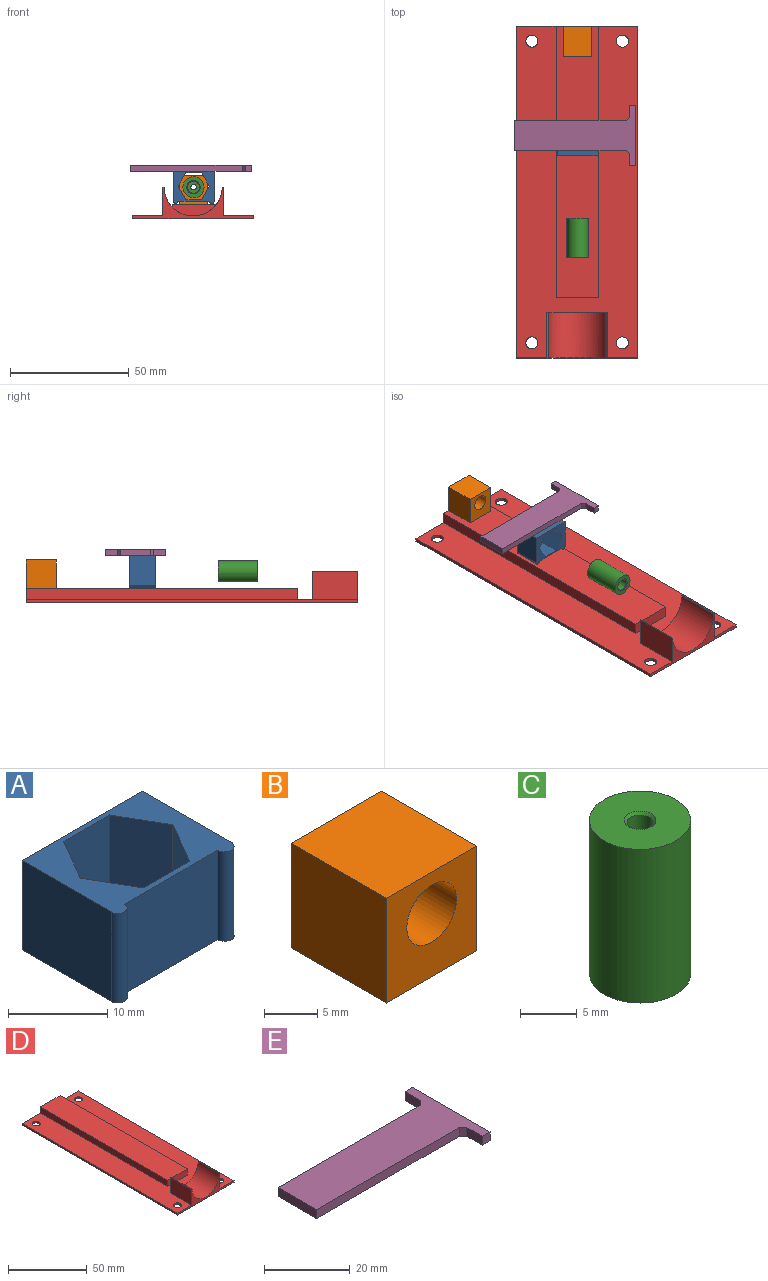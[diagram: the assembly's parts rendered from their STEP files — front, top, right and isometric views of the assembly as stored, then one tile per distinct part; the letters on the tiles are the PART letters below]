
ASSEMBLY  parts=5 mates=4
PART A: 14 faces, bbox 17.1x13.7x11 mm
  f0: plane 17.15x11.05mm, normal (0,1,0), area 189.4mm2, adj f1,f11,f12,f13
  f1: plane 12.7x11.05mm, normal (-1,0,0), area 140.3mm2, adj f0,f2,f12,f13
  f2: cylinder r=0.95mm len=11.05mm, axis (0,0,-1), area 33.1mm2, adj f1,f3,f12,f13
  f3: plane 13.34x11.05mm, normal (0,-1,0), area 147.3mm2, adj f2,f4,f12,f13
  f4: cylinder r=0.95mm len=11.05mm, axis (0,0,-1), area 33.1mm2, adj f3,f11,f12,f13
  f5: plane 11.05x5.72mm, normal (-0.87,0.5,0), area 72.9mm2, adj f6,f10,f12,f13
  f6: plane 11.05x6.6mm, normal (0,1,0), area 72.9mm2, adj f5,f7,f12,f13
  f7: plane 11.05x5.72mm, normal (0.87,0.5,0), area 72.9mm2, adj f6,f8,f12,f13
  f8: plane 11.05x5.72mm, normal (0.87,-0.5,0), area 72.9mm2, adj f7,f9,f12,f13
  f9: plane 11.05x6.6mm, normal (0,-1,0), area 72.9mm2, adj f8,f10,f12,f13
  f10: plane 11.05x5.72mm, normal (-0.87,-0.5,0), area 72.9mm2, adj f5,f9,f12,f13
  f11: plane 12.7x11.05mm, normal (1,0,0), area 140.3mm2, adj f0,f4,f12,f13
  f12: plane 17.15x13.65mm, normal (0,0,1), area 107.4mm2, adj f0,f1,f2,f3,f4,f5,f6,f7
  f13: plane 17.15x13.65mm, normal (0,0,-1), area 107.4mm2, adj f0,f1,f2,f3,f4,f5,f6,f7
PART B: 7 faces, bbox 12.1x12.7x12.1 mm
  f0: plane 12.7x12.07mm, normal (-1,0,0), area 153.2mm2, adj f1,f3,f4,f5
  f1: plane 12.7x12.07mm, normal (0,0,-1), area 153.2mm2, adj f0,f2,f4,f5
  f2: plane 12.7x12.07mm, normal (1,0,0), area 153.2mm2, adj f1,f3,f4,f5
  f3: plane 12.7x12.07mm, normal (0,0,1), area 153.2mm2, adj f0,f2,f4,f5
  f4: plane 12.07x12.07mm, normal (0,-1,0), area 111.3mm2, adj f0,f1,f2,f3,f6
  f5: plane 12.07x12.07mm, normal (0,1,0), area 111.3mm2, adj f0,f1,f2,f3,f6
  f6: cylinder r=3.3mm len=12.7mm, axis (0,-1,0), area 263.5mm2, adj f4,f5
PART C: 8 faces, bbox 8.9x8.9x16.5 mm
  f0: cylinder r=4.45mm len=16.51mm, axis (0,0,-1), area 461.1mm2, adj f2,f3
  f1: cylinder r=1.14mm len=3.56mm, axis (0,0,-1), area 25.5mm2, adj f5,f7
  f2: plane 8.89x8.89mm, normal (0,0,1), area 55.9mm2, adj f0,f7
  f3: plane 8.89x8.89mm, normal (0,0,-1), area 37.5mm2, adj f0,f6
  f4: cylinder r=2.54mm len=12.45mm, axis (0,0,1), area 198.6mm2, adj f5,f6
  f5: plane 5.08x5.08mm, normal (0,0,-1), area 16.2mm2, adj f1,f4
  f6: cone r=2.79mm half-angle=45deg, axis (0,0,-1), area 6mm2, adj f3,f4
  f7: cone r=1.14mm half-angle=45deg, axis (0,0,1), area 2.9mm2, adj f1,f2
PART D: 21 faces, bbox 50.8x139.7x13.3 mm
  f0: plane 139.7x50.8mm, normal (0,0,1), area 4499.6mm2, adj f2,f3,f4,f5,f6,f8,f9,f10
  f1: plane 19.05x0.45mm, normal (0,0,1), area 8.5mm2, adj f2,f3,f10,f12
  f2: plane 50.8x13.34mm, normal (0,-1,0), area 139.7mm2, adj f0,f1,f5,f6,f7,f9,f10,f11
  f3: plane 12.7x12.07mm, normal (0,1,0), area 37.6mm2, adj f0,f1,f10,f12
  f4: plane 50.8x6.03mm, normal (0,1,0), area 149.2mm2, adj f0,f5,f6,f7,f13,f15,f16
  f5: plane 139.7x1.27mm, normal (-1,0,0), area 177.4mm2, adj f0,f2,f4,f7
  f6: plane 139.7x1.27mm, normal (1,0,0), area 177.4mm2, adj f0,f2,f4,f7
  f7: plane 139.7x50.8mm, normal (0,0,-1), area 7015.7mm2, adj f2,f4,f5,f6,f17,f18,f19,f20
  f8: plane 12.7x12.07mm, normal (0,1,0), area 37.6mm2, adj f0,f9,f11,f12
  f9: plane 19.05x12.07mm, normal (-1,0,0), area 229.8mm2, adj f0,f2,f8,f11
  f10: plane 19.05x12.07mm, normal (1,0,0), area 229.8mm2, adj f0,f1,f2,f3
  f11: plane 19.05x0.45mm, normal (0,0,1), area 8.5mm2, adj f2,f8,f9,f12
  f12: cylinder r=12.26mm len=24.51mm, axis (0,-1,0), area 726.2mm2, adj f1,f2,f3,f8,f11
  f13: plane 114.3x4.76mm, normal (-1,0,0), area 544.4mm2, adj f0,f4,f14,f16
  f14: plane 17.78x4.76mm, normal (0,-1,0), area 84.7mm2, adj f0,f13,f15,f16
  f15: plane 114.3x4.76mm, normal (1,0,0), area 544.4mm2, adj f0,f4,f14,f16
  f16: plane 114.3x17.78mm, normal (0,0,1), area 2032.3mm2, adj f4,f13,f14,f15
  f17: cylinder r=2.54mm len=5.08mm, axis (0,0,1), area 20.3mm2, adj f0,f7
  f18: cylinder r=2.54mm len=5.08mm, axis (0,0,1), area 20.3mm2, adj f0,f7
  f19: cylinder r=2.54mm len=5.08mm, axis (0,0,1), area 20.3mm2, adj f0,f7
  f20: cylinder r=2.54mm len=5.08mm, axis (0,0,1), area 20.3mm2, adj f0,f7
PART E: 12 faces, bbox 50.8x25.4x2.5 mm
  f0: plane 5.08x2.54mm, normal (-1,0,0), area 12.9mm2, adj f1,f8,f9,f10
  f1: plane 2.54x2.54mm, normal (0,-1,0), area 6.5mm2, adj f0,f2,f8,f9
  f2: plane 25.4x2.54mm, normal (1,0,0), area 64.5mm2, adj f1,f3,f8,f9
  f3: plane 2.54x2.54mm, normal (0,1,0), area 6.5mm2, adj f2,f4,f8,f9
  f4: plane 5.08x2.54mm, normal (-1,0,0), area 12.9mm2, adj f3,f8,f9,f11
  f5: plane 46.99x2.54mm, normal (0,1,0), area 119.4mm2, adj f6,f8,f9,f11
  f6: plane 12.7x2.54mm, normal (-1,0,0), area 32.3mm2, adj f5,f7,f8,f9
  f7: plane 46.99x2.54mm, normal (0,-1,0), area 119.4mm2, adj f6,f8,f9,f10
  f8: plane 50.8x25.4mm, normal (0,0,1), area 679mm2, adj f0,f1,f2,f3,f4,f5,f6,f7
  f9: plane 50.8x25.4mm, normal (0,0,-1), area 679mm2, adj f0,f1,f2,f3,f4,f5,f6,f7
  f10: plane 2.54x1.27mm, normal (-0.71,-0.71,0), area 4.6mm2, adj f0,f7,f8,f9
  f11: plane 2.54x1.27mm, normal (-0.71,0.71,0), area 4.6mm2, adj f4,f5,f8,f9
PLACE A rot(axis=(1,0,0),90deg) t=(0.04,-1.69,4.89)mm
PLACE B t=(-0.05,35.43,-2.86)mm
PLACE C rot(axis=(-1,0,0),90deg) t=(-0.05,-47.38,4.44)mm
PLACE D t=(-0.2,-28.07,-8.89)mm
PLACE E t=(-1.16,-4.23,11.24)mm
MATE planar D.f4 <-> B.f5  axis (0,1,0) through (-0.2,41.78,-6.55)mm
MATE slider C.f0 <-> B.f6  axis (0,-1,0) through (-0.05,-39.13,4.44)mm
MATE planar D.f16 <-> B.f1  axis (0,0,1) through (-0.2,-15.37,-2.86)mm
MATE planar A.f0 <-> E.f9  axis (0,0,1) through (0.04,-7.22,11.24)mm
